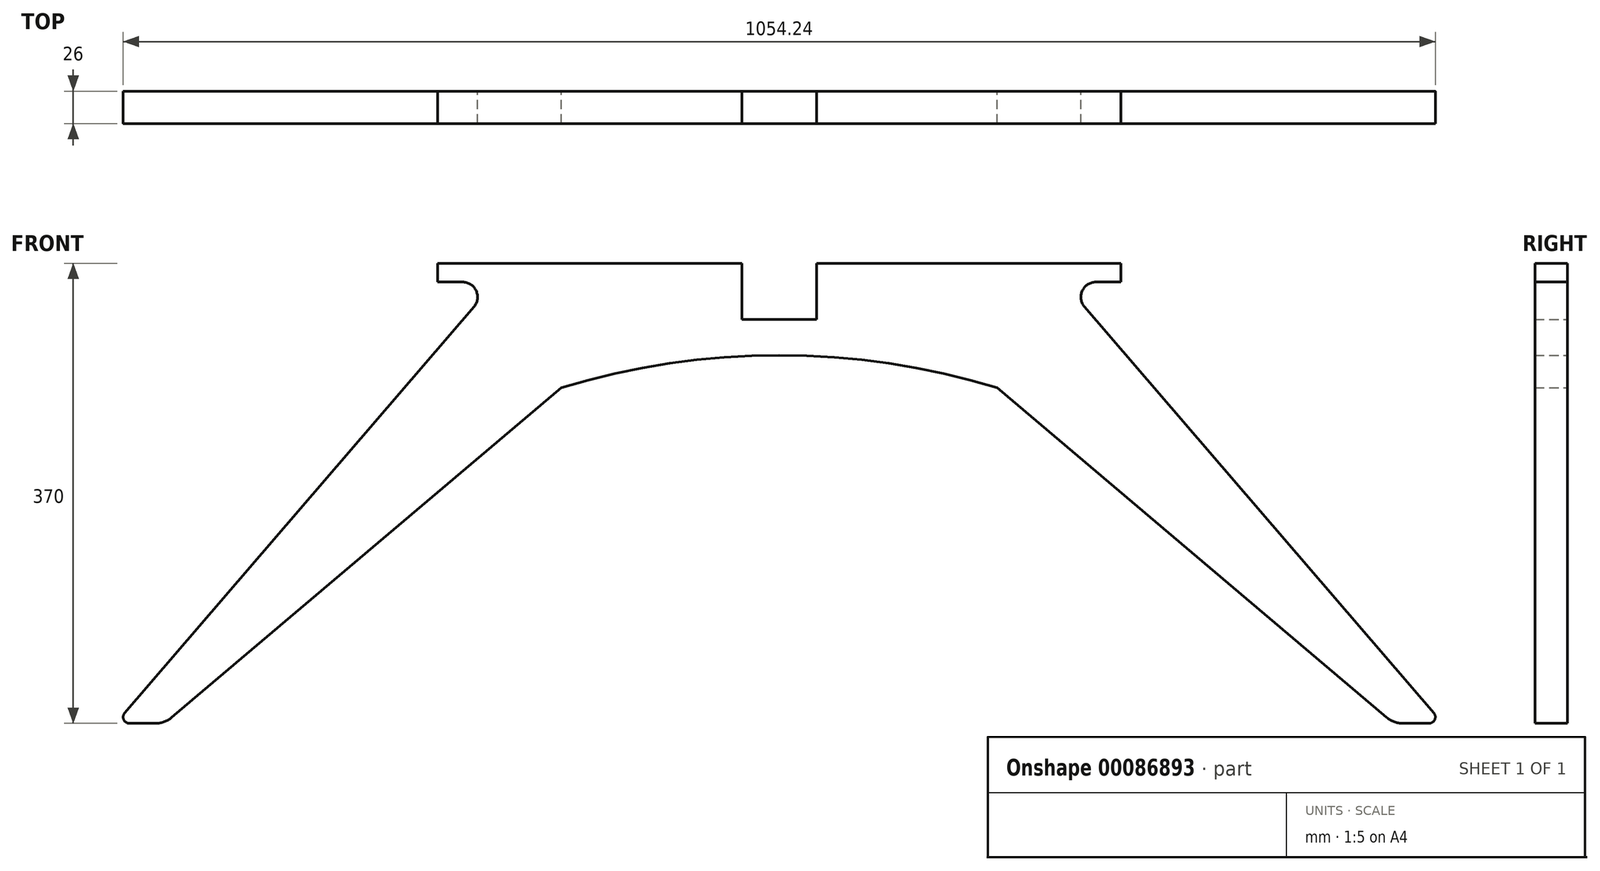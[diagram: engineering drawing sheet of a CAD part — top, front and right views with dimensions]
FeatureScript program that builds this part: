
annotation { "Feature Type Name" : "Feature", "Feature Type Description" : "" }
export const myFeature = defineFeature(function(context is Context, id is Id, definition is map)
    precondition{}
    {
        {
            var Q0;
            Q0=qCreatedBy(makeId("Front.planeOp"),FACE);
            var sketch = newSketch(context, id + "F0", { "sketchPlane" : qUnion([Q0])});
            skLineSegment(sketch, "E0", {"start": v(525.9, -361.74) * mm, "end": v(245.31, -35) * mm});
            skLineSegment(sketch, "E1", {"start": v(522.12, -370) * mm, "end": v(500.93, -370) * mm});
            skLineSegment(sketch, "E2", {"start": v(533, 383.5) * mm, "end": v(533, -561.05) * mm, "construction": true});
            skPoint(sketch, "E3.visualSharp", {"position": v(533, -370) * mm});
            skArc(sketch, "E3.filletArc", {"start": v(522.12, -370) * mm, "mid": v(526.66, -367.09) * mm, "end": v(525.9, -361.74) * mm});
            skArc(sketch, "E4", {"start": v(500.93, -370) * mm, "mid": v(494.04, -368.78) * mm, "end": v(488, -365.26) * mm});
            skPoint(sketch, "E5.orphan", {"position": v(493, -370) * mm});
            skLineSegment(sketch, "E6", {"start": v(-533, 568.71) * mm, "end": v(-533, -664.54) * mm, "construction": true});
            skLineSegment(sketch, "E7", {"start": v(0, -665.77) * mm, "end": v(0, 567.49) * mm, "construction": true});
            skArc(sketch, "E8.MirrorCS", {"start": v(-522.12, -370) * mm, "mid": v(-526.66, -367.09) * mm, "end": v(-525.9, -361.74) * mm});
            skLineSegment(sketch, "E9.MirrorCS", {"start": v(-522.12, -370) * mm, "end": v(-500.93, -370) * mm});
            skArc(sketch, "E10.MirrorCS", {"start": v(-500.93, -370) * mm, "mid": v(-494.04, -368.78) * mm, "end": v(-488, -365.26) * mm});
            skPoint(sketch, "E11.MirrorP", {"position": v(-493, -370) * mm});
            skLineSegment(sketch, "E12.MirrorCS", {"start": v(-525.9, -361.74) * mm, "end": v(-245.31, -35) * mm});
            skPoint(sketch, "E13.MirrorP", {"position": v(-533, -370) * mm});
            skLineSegment(sketch, "E14", {"start": v(488, -365.26) * mm, "end": v(175, -100) * mm});
            skLineSegment(sketch, "E15", {"start": v(-488, -365.26) * mm, "end": v(-175, -100) * mm});
            skLineSegment(sketch, "E16.bottom", {"start": v(-571.7, 18.68) * mm, "end": v(648.3, 18.68) * mm, "construction": true});
            skLineSegment(sketch, "E16.top", {"start": v(-571.7, -591.32) * mm, "end": v(648.3, -591.32) * mm, "construction": true});
            skLineSegment(sketch, "E16.left", {"start": v(-571.7, 18.68) * mm, "end": v(-571.7, -591.32) * mm, "construction": true});
            skLineSegment(sketch, "E16.right", {"start": v(648.3, 18.68) * mm, "end": v(648.3, -591.32) * mm, "construction": true});
            skArc(sketch, "E17", {"start": v(245.31, -35) * mm, "mid": v(243.5, -22.06) * mm, "end": v(254.5, -15) * mm});
            skLineSegment(sketch, "E18", {"start": v(254.5, -15) * mm, "end": v(274.5, -15) * mm});
            skLineSegment(sketch, "E19", {"start": v(274.5, -15) * mm, "end": v(274.5, 0) * mm});
            skLineSegment(sketch, "E20", {"start": v(274.5, 0) * mm, "end": v(30, 0) * mm});
            skLineSegment(sketch, "E21", {"start": v(-274.5, 0) * mm, "end": v(-274.5, -15) * mm});
            skLineSegment(sketch, "E22", {"start": v(-274.5, -15) * mm, "end": v(-254.5, -15) * mm});
            skArc(sketch, "E23", {"start": v(-254.5, -15) * mm, "mid": v(-243.5, -22.06) * mm, "end": v(-245.31, -35) * mm});
            skPoint(sketch, "E24", {"position": v(0, 0) * mm});
            skArc(sketch, "E25", {"start": v(-175, -100) * mm, "mid": v(-103.28, -82.87) * mm, "end": v(-30, -74.66) * mm});
            skLineSegment(sketch, "E26.top", {"start": v(-30, -45) * mm, "end": v(30, -45) * mm});
            skLineSegment(sketch, "E26.left", {"start": v(-30, -74.66) * mm, "end": v(-30, -45) * mm, "construction": true});
            skLineSegment(sketch, "E26.right", {"start": v(30, -74.66) * mm, "end": v(30, -45) * mm, "construction": true});
            skPoint(sketch, "E27", {"position": v(0, -45) * mm});
            skArc(sketch, "E28.trimOffspring", {"start": v(30, -74.66) * mm, "mid": v(103.28, -82.87) * mm, "end": v(175, -100) * mm});
            skLineSegment(sketch, "E29", {"start": v(-30, -45) * mm, "end": v(-30, 0) * mm});
            skLineSegment(sketch, "E30", {"start": v(30, -45) * mm, "end": v(30, 0) * mm});
            skLineSegment(sketch, "E31.trimOffspring", {"start": v(-30, 0) * mm, "end": v(-274.5, 0) * mm});
            skArc(sketch, "E32", {"start": v(-30, -74.66) * mm, "mid": v(0, -73.91) * mm, "end": v(30, -74.66) * mm});
            skSolve(sketch);
        }
        {
            var Q0;
            Q0=qSketchRegion(id+"F0",true);
            extrude(context, id + "F1", {"entities" : qUnion([Q0]), "depth" : 26 * mm});
        }
    });
